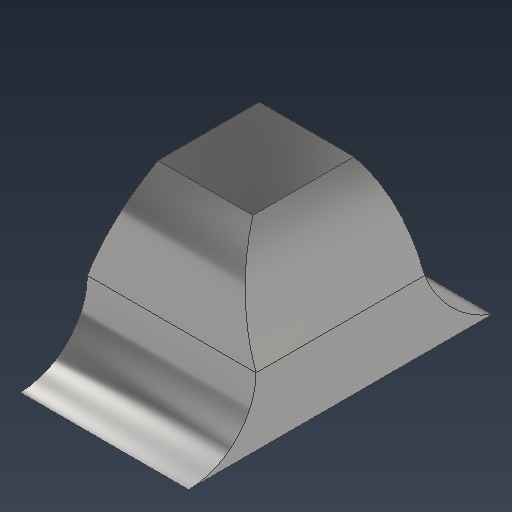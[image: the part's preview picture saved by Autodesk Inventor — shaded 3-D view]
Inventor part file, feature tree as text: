
AUTODESK INVENTOR PART (.ipt)
format: ipt  version: 2021 (Build 250183000, 183)  size: 176,128 bytes
history: native  units: mm
features: extrude x3, sketch x3, mirror x1
ambient origin geometry x8: Origin, YZ Plane, XZ Plane, XY Plane, X Axis, Y Axis, Z Axis, Center Point
bodies: Solid1 (feature_tree)
feature tree (7):
  extrude  "Extrusion1"  Depth=4.0mm
  mirror  "Mirror1"
  extrude  "Extrusion3"  Depth=10.0mm TaperAngle=0.0deg
  extrude  "Extrusion4"  Depth=10.0mm
  sketch  "Sketch1"  dims[d0=4.0mm d1=6.0mm]
  sketch  "Sketch2"  dims[d2=5.0mm d3=10.0mm d4=0.0mm]
  sketch  "Sketch3"  dims[d7=10.0mm d8=8.0mm d11=10.0mm d12=8.0mm d13=10.0mm d14=0.0mm d15=4.0mm d16=7.0mm d17=7.0mm d18=4.0mm d19=10.0mm d20=0.0mm]
